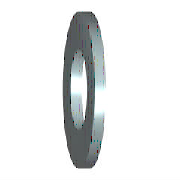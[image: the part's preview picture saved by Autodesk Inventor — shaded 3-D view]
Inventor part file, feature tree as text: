
AUTODESK INVENTOR PART (.ipt)
format: ipt  version: 2023 (Build 270158000, 158)  size: 104,960 bytes
history: native  units: mm (DEFAULTED — no unit token found)
features: extrude x1, other x1, plane x1, sketch x1
ambient origin geometry x7: Origin, YZ Plane, XY Plane, X Axis, Y Axis, Z Axis, Center Point
bodies: Solid1 (feature_tree)
feature tree (4):
  extrude  "Corpo"  Depth=20.0mm
  other  "Work Axis1"
  plane  "Work Plane1"
  sketch  "Schizzo"
